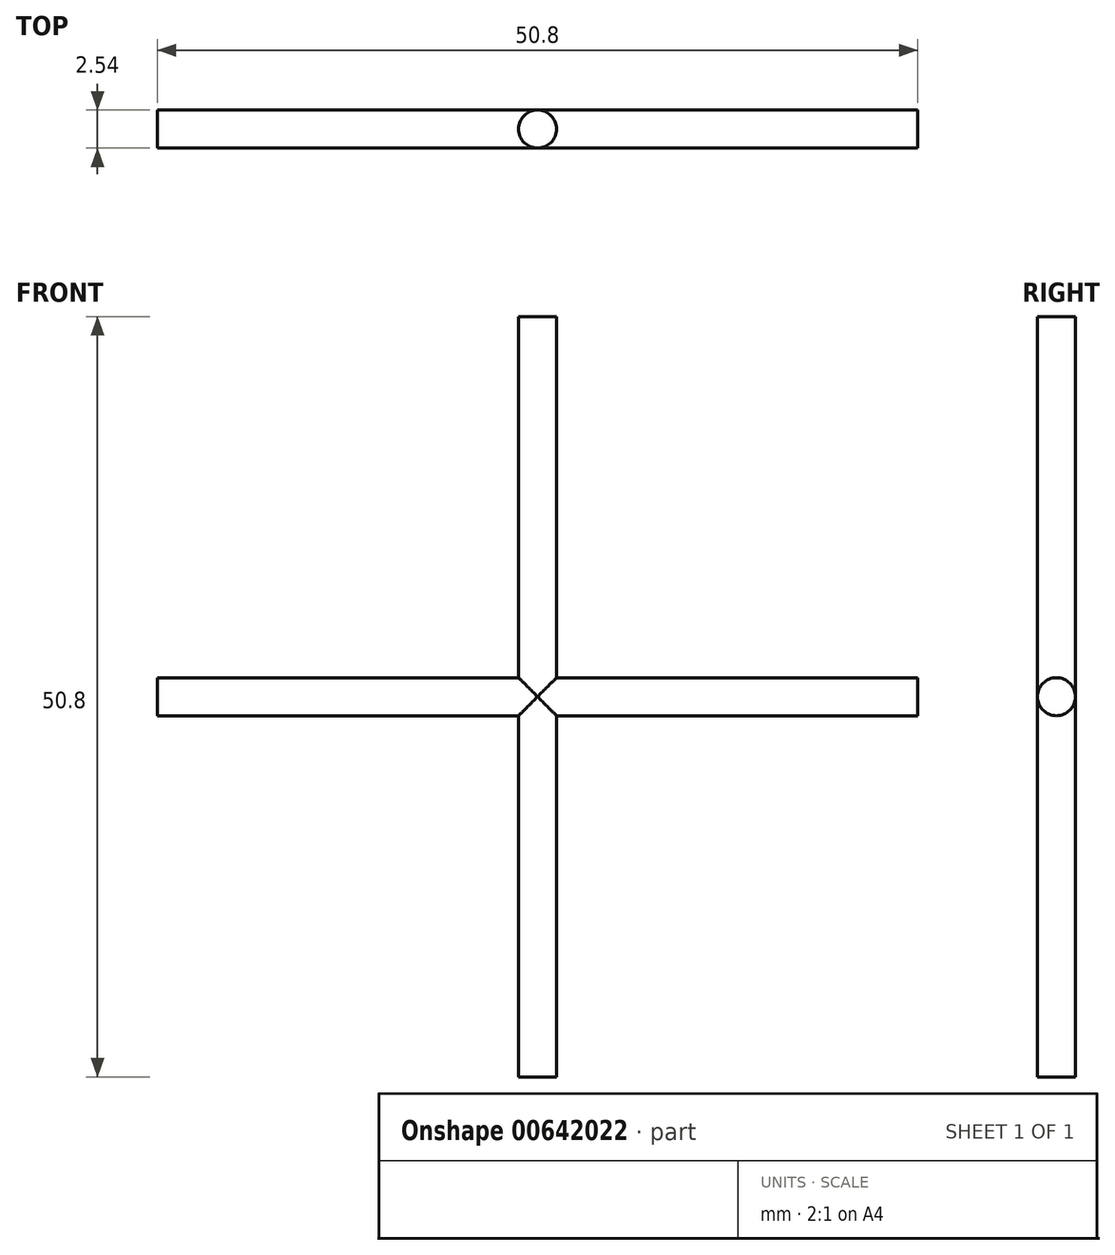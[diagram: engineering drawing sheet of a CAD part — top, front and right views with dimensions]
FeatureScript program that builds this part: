
annotation { "Feature Type Name" : "Feature", "Feature Type Description" : "" }
export const myFeature = defineFeature(function(context is Context, id is Id, definition is map)
    precondition{}
    {
        {
            var Q0;
            Q0=qCreatedBy(makeId("Top.planeOp"),FACE);
            var sketch = newSketch(context, id + "F0", { "sketchPlane" : qUnion([Q0])});
            skCircle(sketch, "E0", {"center": v(0, 0) * mm, "radius": 1.27 * mm});
            skSolve(sketch);
        }
        {
            var Q0;
            Q0 = qSketchRegion(id + "F0", true);
            extrude(context, id + "F1", {"entities" : qUnion([Q0]), "depth" : 25.4 * mm, "offsetDistance" : 25.4 * mm, "hasSecondDirection" : true, "secondDirectionOppositeDirection" : true, "secondDirectionDepth" : 25.4 * mm});
        }
        {
            var Q0;
            Q0=qCreatedBy(makeId("Right.planeOp"),FACE);
            var sketch = newSketch(context, id + "F2", { "sketchPlane" : qUnion([Q0])});
            skCircle(sketch, "E1", {"center": v(0, 0) * mm, "radius": 1.27 * mm});
            skSolve(sketch);
        }
        {
            var Q0;
            Q0 = qSketchRegion(id + "F2", true);
            extrude(context, id + "F3", {"entities" : qUnion([Q0]), "operationType" : NewBodyOperationType.ADD, "depth" : 25.4 * mm, "offsetDistance" : 25.4 * mm, "hasSecondDirection" : true, "secondDirectionOppositeDirection" : true, "secondDirectionDepth" : 25.4 * mm});
        }
    });
